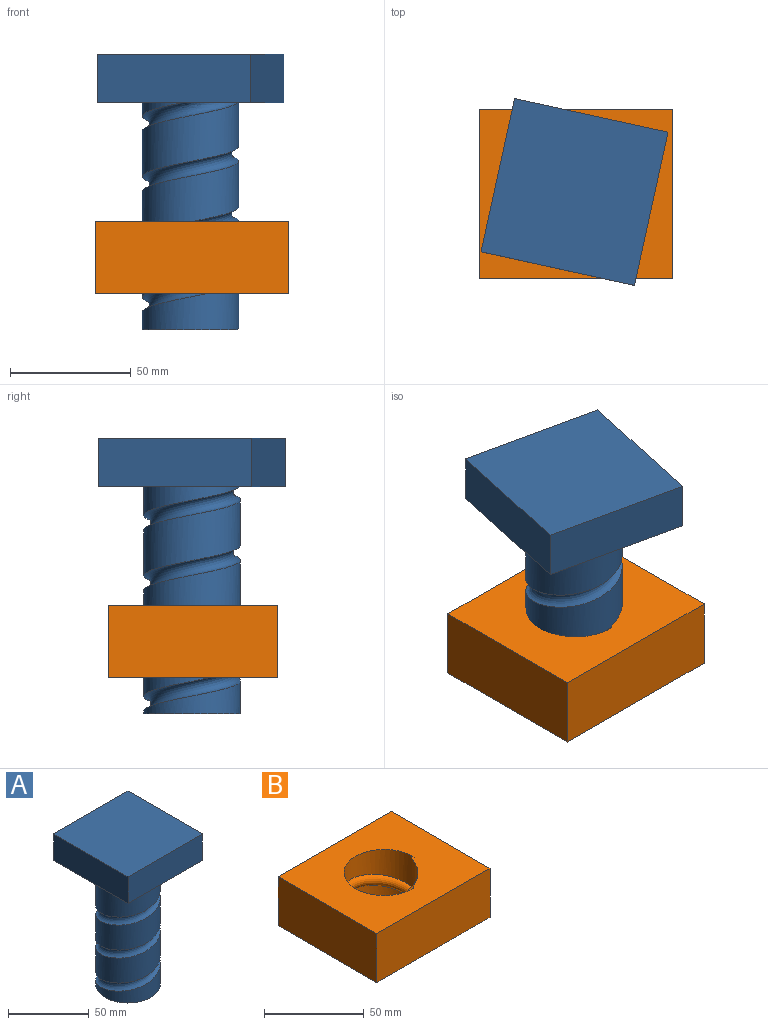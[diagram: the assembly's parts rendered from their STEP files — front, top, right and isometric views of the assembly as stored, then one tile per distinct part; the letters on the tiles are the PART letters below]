
ASSEMBLY  parts=2 mates=1
PART A: 9 faces, bbox 65x65x119.9 mm
  f0: cylinder r=20mm len=94mm, axis (0,0,-1), area 8957.5mm2, adj f1,f2,f3
  f1: plane 40x40mm, normal (0,0,-1), area 1188.7mm2, adj f0,f2
  f2: bspline ~105.88x42.06mm, area 4114.4mm2, adj f0,f1,f3
  f3: plane 65x65mm, normal (0,0,-1), area 3036.3mm2, adj f0,f2,f4,f5,f6,f7
  f4: plane 65x20mm, normal (1,0,0), area 1300mm2, adj f3,f5,f7,f8
  f5: plane 65x20mm, normal (0,1,0), area 1300mm2, adj f3,f4,f6,f8
  f6: plane 65x20mm, normal (-1,0,0), area 1300mm2, adj f3,f5,f7,f8
  f7: plane 65x20mm, normal (0,-1,0), area 1300mm2, adj f3,f4,f6,f8
  f8: plane 65x65mm, normal (0,0,1), area 4225mm2, adj f4,f5,f6,f7
PART B: 8 faces, bbox 80x70x43.4 mm
  f0: plane 80x70mm, normal (0,0,-1), area 4411.3mm2, adj f1,f2,f3,f4,f6,f7
  f1: plane 70x30mm, normal (1,0,0), area 2100mm2, adj f0,f2,f4,f5
  f2: plane 80x30mm, normal (0,1,0), area 2400mm2, adj f0,f1,f3,f5
  f3: plane 70x30mm, normal (-1,0,0), area 2100mm2, adj f0,f2,f4,f5
  f4: plane 80x30mm, normal (0,-1,0), area 2400mm2, adj f0,f1,f3,f5
  f5: plane 80x70mm, normal (0,0,1), area 4411.2mm2, adj f1,f2,f3,f4,f6,f7
  f6: cylinder r=20mm len=40mm, axis (0,0,-1), area 2847.4mm2, adj f0,f5,f7
  f7: bspline ~43.38x42.06mm, area 1313.4mm2, adj f0,f5,f6
PLACE A rot(axis=(0,0,-1),12.4deg) t=(-0.61,0.57,49.14)mm
PLACE B at identity fixed
MATE cylindrical B.f5 <-> A.f0  axis (0,0,1) through (-0.61,0.57,30)mm
